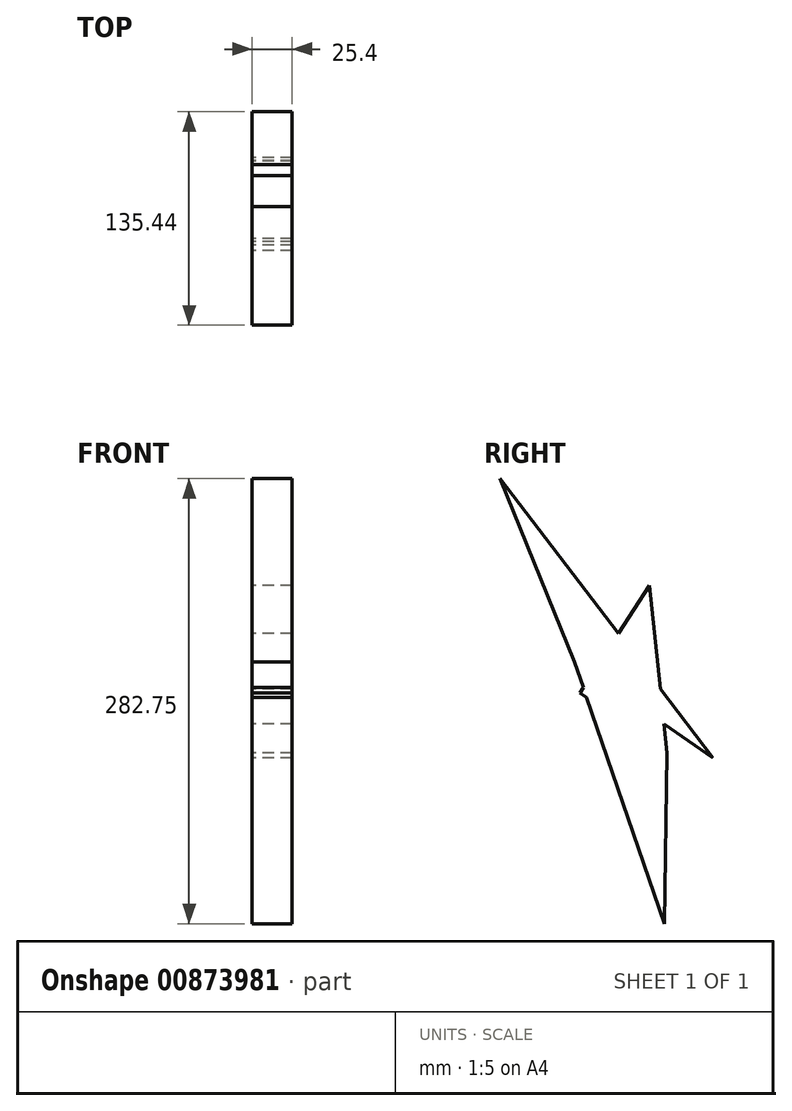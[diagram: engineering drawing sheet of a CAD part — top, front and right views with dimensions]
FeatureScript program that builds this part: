
annotation { "Feature Type Name" : "Feature", "Feature Type Description" : "" }
export const myFeature = defineFeature(function(context is Context, id is Id, definition is map)
    precondition{}
    {
        {
            var Q0;
            Q0=qCreatedBy(makeId("Right.planeOp"),FACE);
            var sketch = newSketch(context, id + "F0", { "sketchPlane" : qUnion([Q0])});
            skLineSegment(sketch, "E0", {"start": v(-36.57, -31.6) * mm, "end": v(18.88, -69.93) * mm});
            skLineSegment(sketch, "E1", {"start": v(18.88, -69.93) * mm, "end": v(7.57, 36.58) * mm});
            skLineSegment(sketch, "E2", {"start": v(7.57, 36.58) * mm, "end": v(-36.57, -31.6) * mm});
            skLineSegment(sketch, "E3", {"start": v(-40, -12.15) * mm, "end": v(48.08, -73.06) * mm});
            skLineSegment(sketch, "E4", {"start": v(48.08, -73.06) * mm, "end": v(-87.36, 104.46) * mm});
            skLineSegment(sketch, "E5", {"start": v(-87.36, 104.46) * mm, "end": v(-40, -12.15) * mm});
            skLineSegment(sketch, "E6", {"start": v(-40, -12.15) * mm, "end": v(17.12, -178.29) * mm});
            skLineSegment(sketch, "E7", {"start": v(17.12, -178.29) * mm, "end": v(18.88, -69.93) * mm});
            skSolve(sketch);
        }
        {
            var Q0;
            Q0 = qSketchRegion(id + "F0", true);
            extrude(context, id + "F1", {"entities" : qUnion([Q0]), "depth" : 25.4 * mm, "offsetDistance" : 25.4 * mm});
        }
    });
